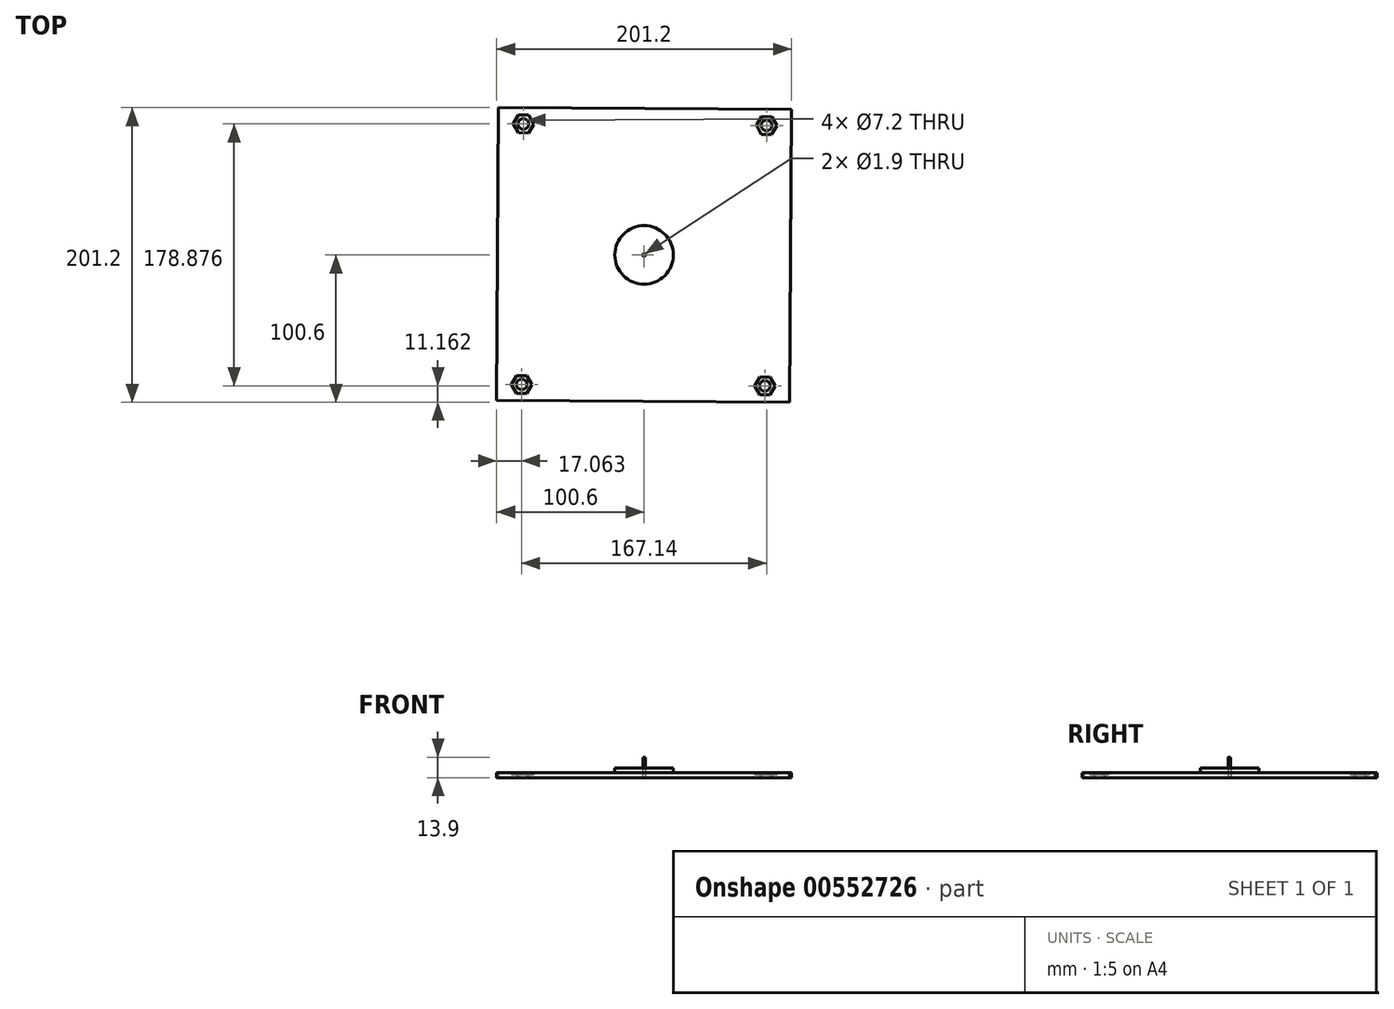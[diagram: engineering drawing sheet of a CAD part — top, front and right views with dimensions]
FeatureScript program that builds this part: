
annotation { "Feature Type Name" : "Feature", "Feature Type Description" : "" }
export const myFeature = defineFeature(function(context is Context, id is Id, definition is map)
    precondition{}
    {
        {
            var Q0;
            Q0=qCreatedBy(makeId("Top.planeOp"),FACE);
            var sketch = newSketch(context, id + "F0", { "sketchPlane" : qUnion([Q0])});
            skLineSegment(sketch, "E0.bottom", {"start": v(-99.4, 100.6) * mm, "end": v(100.6, 99.4) * mm});
            skLineSegment(sketch, "E0.top", {"start": v(-100.6, -99.4) * mm, "end": v(99.4, -100.6) * mm});
            skLineSegment(sketch, "E0.left", {"start": v(-99.4, 100.6) * mm, "end": v(-100.6, -99.4) * mm});
            skLineSegment(sketch, "E0.right", {"start": v(100.6, 99.4) * mm, "end": v(99.4, -100.6) * mm});
            skCircle(sketch, "E1.cCircle", {"center": v(-83.54, -88.43) * mm, "radius": 6.06 * mm, "construction": true});
            skLineSegment(sketch, "E1.0", {"start": v(-90.54, -88.4) * mm, "end": v(-87.07, -94.47) * mm});
            skLineSegment(sketch, "E1.1", {"start": v(-87, -82.35) * mm, "end": v(-90.54, -88.4) * mm});
            skLineSegment(sketch, "E1.2", {"start": v(-80, -82.4) * mm, "end": v(-87, -82.35) * mm});
            skLineSegment(sketch, "E1.3", {"start": v(-76.54, -88.48) * mm, "end": v(-80, -82.4) * mm});
            skLineSegment(sketch, "E1.4", {"start": v(-80.07, -94.52) * mm, "end": v(-76.54, -88.48) * mm});
            skLineSegment(sketch, "E1.5", {"start": v(-87.07, -94.47) * mm, "end": v(-80.07, -94.52) * mm});
            skPoint(sketch, "E1.0.midPoint", {"position": v(-88.8, -91.43) * mm});
            skCircle(sketch, "E2", {"center": v(-83.54, -88.43) * mm, "radius": 3.6 * mm});
            skCircle(sketch, "E3.cCircle", {"center": v(-82.4, 89.44) * mm, "radius": 6.06 * mm, "construction": true});
            skLineSegment(sketch, "E3.0", {"start": v(-75.4, 89.4) * mm, "end": v(-78.93, 83.35) * mm});
            skLineSegment(sketch, "E3.1", {"start": v(-78.93, 83.35) * mm, "end": v(-85.93, 83.4) * mm});
            skLineSegment(sketch, "E3.2", {"start": v(-85.93, 83.4) * mm, "end": v(-89.4, 89.48) * mm});
            skLineSegment(sketch, "E3.3", {"start": v(-89.4, 89.48) * mm, "end": v(-85.86, 95.52) * mm});
            skLineSegment(sketch, "E3.4", {"start": v(-85.86, 95.52) * mm, "end": v(-78.86, 95.48) * mm});
            skLineSegment(sketch, "E3.5", {"start": v(-78.86, 95.48) * mm, "end": v(-75.4, 89.4) * mm});
            skPoint(sketch, "E3.0.midPoint", {"position": v(-77.16, 86.38) * mm});
            skCircle(sketch, "E4", {"center": v(-82.4, 89.44) * mm, "radius": 3.6 * mm});
            skCircle(sketch, "E5.cCircle", {"center": v(83.6, 88.43) * mm, "radius": 6.06 * mm, "construction": true});
            skLineSegment(sketch, "E5.0", {"start": v(90.6, 88.4) * mm, "end": v(87.07, 82.35) * mm});
            skLineSegment(sketch, "E5.1", {"start": v(87.07, 82.35) * mm, "end": v(80.07, 82.4) * mm});
            skLineSegment(sketch, "E5.2", {"start": v(80.07, 82.4) * mm, "end": v(76.6, 88.48) * mm});
            skLineSegment(sketch, "E5.3", {"start": v(76.6, 88.48) * mm, "end": v(80.14, 94.52) * mm});
            skLineSegment(sketch, "E5.4", {"start": v(80.14, 94.52) * mm, "end": v(87.14, 94.47) * mm});
            skLineSegment(sketch, "E5.5", {"start": v(87.14, 94.47) * mm, "end": v(90.6, 88.4) * mm});
            skPoint(sketch, "E5.0.midPoint", {"position": v(88.83, 85.37) * mm});
            skCircle(sketch, "E6", {"center": v(83.6, 88.43) * mm, "radius": 3.6 * mm});
            skCircle(sketch, "E7.cCircle", {"center": v(82.4, -89.44) * mm, "radius": 6.06 * mm, "construction": true});
            skLineSegment(sketch, "E7.0", {"start": v(89.4, -89.48) * mm, "end": v(85.86, -95.52) * mm});
            skLineSegment(sketch, "E7.1", {"start": v(85.86, -95.52) * mm, "end": v(78.86, -95.48) * mm});
            skLineSegment(sketch, "E7.2", {"start": v(78.86, -95.48) * mm, "end": v(75.4, -89.4) * mm});
            skLineSegment(sketch, "E7.3", {"start": v(75.4, -89.4) * mm, "end": v(78.93, -83.35) * mm});
            skLineSegment(sketch, "E7.4", {"start": v(78.93, -83.35) * mm, "end": v(85.93, -83.4) * mm});
            skLineSegment(sketch, "E7.5", {"start": v(85.93, -83.4) * mm, "end": v(89.4, -89.48) * mm});
            skPoint(sketch, "E7.0.midPoint", {"position": v(87.62, -92.5) * mm});
            skCircle(sketch, "E8", {"center": v(82.4, -89.44) * mm, "radius": 3.6 * mm});
            skCircle(sketch, "E9", {"center": v(0, 0) * mm, "radius": 0.95 * mm});
            skSolve(sketch);
        }
        {
            var Q0;
            Q0=makeQuery(id+"F0.imprint","IMPRINT",FACE,{"disambiguationData":[TD([[makeQuery(id+"F0.imprint","IMPRINT",EDGE,{"derivedFrom":sQuery(id+"F0.wireOp",EDGE,"E0.bottom")}),-1.0]])]});
            extrude(context, id + "F1", {"entities" : qUnion([Q0]), "depth" : 3.2 * mm});
        }
        {
            var Q0;
            Q0=makeQuery(id+"F0.imprint","IMPRINT",FACE,{"disambiguationData":[TD([[makeQuery(id+"F0.imprint","IMPRINT",EDGE,{"derivedFrom":sQuery(id+"F0.wireOp",EDGE,"E1.0")}),1.0]])]});
            var Q1;
            Q1=makeQuery(id+"F0.imprint","IMPRINT",FACE,{"disambiguationData":[TD([[makeQuery(id+"F0.imprint","IMPRINT",EDGE,{"derivedFrom":sQuery(id+"F0.wireOp",EDGE,"E3.0")}),-1.0]])]});
            var Q2;
            Q2=makeQuery(id+"F0.imprint","IMPRINT",FACE,{"disambiguationData":[TD([[makeQuery(id+"F0.imprint","IMPRINT",EDGE,{"derivedFrom":sQuery(id+"F0.wireOp",EDGE,"E7.0")}),-1.0]])]});
            var Q3;
            Q3=makeQuery(id+"F0.imprint","IMPRINT",FACE,{"disambiguationData":[TD([[makeQuery(id+"F0.imprint","IMPRINT",EDGE,{"derivedFrom":sQuery(id+"F0.wireOp",EDGE,"E5.0")}),-1.0]])]});
            extrude(context, id + "F2", {"entities" : qUnion([Q0, Q1, Q2, Q3]), "operationType" : NewBodyOperationType.ADD, "depth" : 2 * mm});
        }
        {
            var Q0;
            Q0=makeQuery(id+"F1.opExtrude","CAP_FACE",FACE,{"disambiguationData":[OSD([sQuery(id+"F0.wireOp",EDGE,"E0.bottom"),sQuery(id+"F0.wireOp",EDGE,"E0.top"),sQuery(id+"F0.wireOp",EDGE,"E0.left"),sQuery(id+"F0.wireOp",EDGE,"E0.right"),sQuery(id+"F0.wireOp",EDGE,"E1.0"),sQuery(id+"F0.wireOp",EDGE,"E1.1"),sQuery(id+"F0.wireOp",EDGE,"E1.2"),sQuery(id+"F0.wireOp",EDGE,"E1.3"),sQuery(id+"F0.wireOp",EDGE,"E1.4"),sQuery(id+"F0.wireOp",EDGE,"E1.5"),sQuery(id+"F0.wireOp",EDGE,"E3.0"),sQuery(id+"F0.wireOp",EDGE,"E3.1"),sQuery(id+"F0.wireOp",EDGE,"E3.2"),sQuery(id+"F0.wireOp",EDGE,"E3.3"),sQuery(id+"F0.wireOp",EDGE,"E3.4"),sQuery(id+"F0.wireOp",EDGE,"E3.5"),sQuery(id+"F0.wireOp",EDGE,"E5.0"),sQuery(id+"F0.wireOp",EDGE,"E5.1"),sQuery(id+"F0.wireOp",EDGE,"E5.2"),sQuery(id+"F0.wireOp",EDGE,"E5.3"),sQuery(id+"F0.wireOp",EDGE,"E5.4"),sQuery(id+"F0.wireOp",EDGE,"E5.5"),sQuery(id+"F0.wireOp",EDGE,"E7.0"),sQuery(id+"F0.wireOp",EDGE,"E7.1"),sQuery(id+"F0.wireOp",EDGE,"E7.2"),sQuery(id+"F0.wireOp",EDGE,"E7.3"),sQuery(id+"F0.wireOp",EDGE,"E7.4"),sQuery(id+"F0.wireOp",EDGE,"E7.5")])],"isStart":false});
            var sketch = newSketch(context, id + "F3", { "sketchPlane" : qUnion([Q0])});
            skCircle(sketch, "E10", {"center": v(0, 0) * mm, "radius": 20 * mm});
            skCircle(sketch, "E11", {"center": v(0, 0) * mm, "radius": 0.95 * mm});
            skSolve(sketch);
        }
        {
            var Q0;
            Q0=makeQuery(id+"F3.imprint","IMPRINT",FACE,{"disambiguationData":[TD([[makeQuery(id+"F3.imprint","IMPRINT",EDGE,{"derivedFrom":sQuery(id+"F3.wireOp",EDGE,"E10")}),1.0]])]});
            extrude(context, id + "F4", {"entities" : qUnion([Q0]), "depth" : 3.2 * mm});
        }
        {
            var Q0;
            Q0=makeQuery(id+"F4.opExtrude","CAP_FACE",FACE,{"disambiguationData":[OSD([sQuery(id+"F3.wireOp",EDGE,"E10"),sQuery(id+"F3.wireOp",EDGE,"E11")])],"isStart":false});
            var sketch = newSketch(context, id + "F5", { "sketchPlane" : qUnion([Q0])});
            skCircle(sketch, "E12", {"center": v(0, 0) * mm, "radius": 0.8 * mm});
            skSolve(sketch);
        }
        {
            var Q0;
            Q0=makeQuery(id+"F5.imprint","IMPRINT",FACE,{"disambiguationData":[TD([[makeQuery(id+"F5.imprint","IMPRINT",EDGE,{"derivedFrom":sQuery(id+"F5.wireOp",EDGE,"E12")}),1.0]])]});
            extrude(context, id + "F6", {"entities" : qUnion([Q0]), "depth" : 7.5 * mm});
        }
    });
